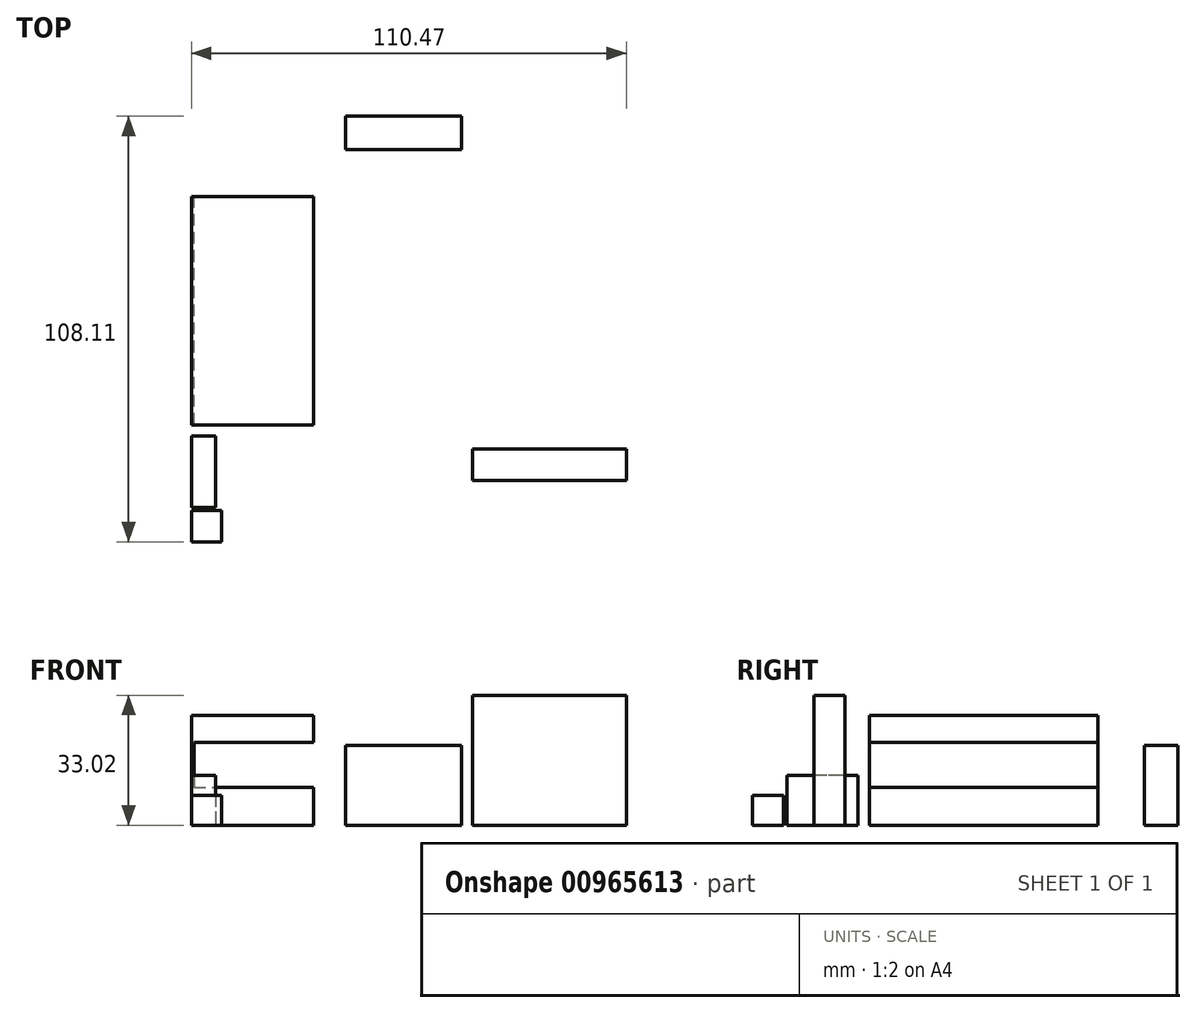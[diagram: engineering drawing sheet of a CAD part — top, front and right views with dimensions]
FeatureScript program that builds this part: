
annotation { "Feature Type Name" : "Feature", "Feature Type Description" : "" }
export const myFeature = defineFeature(function(context is Context, id is Id, definition is map)
    precondition{}
    {
        {
            var Q0;
            Q0=qCreatedBy(makeId("Top.planeOp"),FACE);
            var sketch = newSketch(context, id + "F0", { "sketchPlane" : qUnion([Q0])});
            skLineSegment(sketch, "E0", {"start": v(-79.8, -55.8) * mm, "end": v(-42.57, -55.8) * mm});
            skLineSegment(sketch, "E1", {"start": v(-42.57, -55.8) * mm, "end": v(-42.57, -57.97) * mm});
            skLineSegment(sketch, "E2", {"start": v(-42.57, -57.97) * mm, "end": v(-14.53, -57.97) * mm});
            skLineSegment(sketch, "E3", {"start": v(-14.53, -57.97) * mm, "end": v(-14.53, -55.8) * mm});
            skLineSegment(sketch, "E4", {"start": v(-14.53, -55.8) * mm, "end": v(-10.05, -55.8) * mm});
            skLineSegment(sketch, "E5", {"start": v(-10.05, -55.8) * mm, "end": v(-10.05, -38.6) * mm});
            skLineSegment(sketch, "E6", {"start": v(-10.05, -38.6) * mm, "end": v(30.69, -38.6) * mm});
            skLineSegment(sketch, "E7", {"start": v(30.69, -38.6) * mm, "end": v(30.69, -30.65) * mm});
            skLineSegment(sketch, "E8", {"start": v(30.69, -30.65) * mm, "end": v(33.75, -30.65) * mm});
            skLineSegment(sketch, "E9", {"start": v(33.75, -30.65) * mm, "end": v(33.75, 18.65) * mm});
            skLineSegment(sketch, "E10", {"start": v(33.75, 18.65) * mm, "end": v(30.69, 18.65) * mm});
            skLineSegment(sketch, "E11", {"start": v(30.69, 18.65) * mm, "end": v(30.69, 53.03) * mm});
            skLineSegment(sketch, "E12.bottom", {"start": v(-79.8, 33.53) * mm, "end": v(-48.74, 33.53) * mm});
            skLineSegment(sketch, "E12.top", {"start": v(-79.8, -24.5) * mm, "end": v(-48.74, -24.5) * mm});
            skLineSegment(sketch, "E12.left", {"start": v(-79.8, 33.53) * mm, "end": v(-79.8, -24.5) * mm});
            skLineSegment(sketch, "E12.right", {"start": v(-48.74, 33.53) * mm, "end": v(-48.74, -24.5) * mm});
            skLineSegment(sketch, "E13.bottom", {"start": v(-79.8, -27.35) * mm, "end": v(-73.64, -27.35) * mm});
            skLineSegment(sketch, "E13.top", {"start": v(-79.8, -45.45) * mm, "end": v(-73.64, -45.45) * mm});
            skLineSegment(sketch, "E13.left", {"start": v(-79.8, -27.35) * mm, "end": v(-79.8, -45.45) * mm});
            skLineSegment(sketch, "E13.right", {"start": v(-73.64, -27.35) * mm, "end": v(-73.64, -45.45) * mm});
            skLineSegment(sketch, "E14.bottom", {"start": v(-79.8, -46.32) * mm, "end": v(-72.1, -46.32) * mm});
            skLineSegment(sketch, "E14.top", {"start": v(-79.8, -54.22) * mm, "end": v(-72.1, -54.22) * mm});
            skLineSegment(sketch, "E14.left", {"start": v(-79.8, -46.32) * mm, "end": v(-79.8, -54.22) * mm});
            skLineSegment(sketch, "E14.right", {"start": v(-72.1, -46.32) * mm, "end": v(-72.1, -54.22) * mm});
            skPoint(sketch, "E15.firstSnap0", {"position": v(-72.1, -50.27) * mm});
            skLineSegment(sketch, "E16.bottom", {"start": v(-8.38, -38.6) * mm, "end": v(30.67, -38.6) * mm});
            skLineSegment(sketch, "E16.top", {"start": v(-8.38, -30.65) * mm, "end": v(30.67, -30.65) * mm});
            skLineSegment(sketch, "E16.left", {"start": v(-8.38, -38.6) * mm, "end": v(-8.38, -30.65) * mm});
            skLineSegment(sketch, "E16.right", {"start": v(30.67, -38.6) * mm, "end": v(30.67, -30.65) * mm});
            skLineSegment(sketch, "E17", {"start": v(-38.33, 54.66) * mm, "end": v(-79.8, 54.66) * mm});
            skLineSegment(sketch, "E18", {"start": v(30.69, 54.66) * mm, "end": v(30.69, 53.03) * mm});
            skLineSegment(sketch, "E19", {"start": v(-38.33, 56.29) * mm, "end": v(2.18, 56.29) * mm});
            skLineSegment(sketch, "E20", {"start": v(2.18, 56.29) * mm, "end": v(2.18, 54.66) * mm});
            skLineSegment(sketch, "E21", {"start": v(2.18, 54.66) * mm, "end": v(30.69, 54.66) * mm});
            skLineSegment(sketch, "E22", {"start": v(-38.33, 56.29) * mm, "end": v(-38.33, 54.66) * mm});
            skLineSegment(sketch, "E23.bottom", {"start": v(-40.63, 53.89) * mm, "end": v(-11.15, 53.89) * mm});
            skLineSegment(sketch, "E23.top", {"start": v(-40.63, 45.44) * mm, "end": v(-11.15, 45.44) * mm});
            skLineSegment(sketch, "E23.left", {"start": v(-40.63, 53.89) * mm, "end": v(-40.63, 45.44) * mm});
            skLineSegment(sketch, "E23.right", {"start": v(-11.15, 53.89) * mm, "end": v(-11.15, 45.44) * mm});
            skLineSegment(sketch, "E24", {"start": v(-79.8, 52.05) * mm, "end": v(-81.38, 52.05) * mm});
            skLineSegment(sketch, "E25", {"start": v(-81.38, 52.05) * mm, "end": v(-81.38, 35.03) * mm});
            skLineSegment(sketch, "E26", {"start": v(-81.38, 35.03) * mm, "end": v(-79.8, 35.03) * mm});
            skLineSegment(sketch, "E27", {"start": v(-79.8, 54.66) * mm, "end": v(-79.8, 52.05) * mm});
            skLineSegment(sketch, "E28", {"start": v(-79.8, 35.03) * mm, "end": v(-79.8, 33.53) * mm});
            skLineSegment(sketch, "E29", {"start": v(-79.8, -24.5) * mm, "end": v(-79.8, -27.35) * mm});
            skLineSegment(sketch, "E30", {"start": v(-79.8, -45.45) * mm, "end": v(-79.8, -46.32) * mm});
            skLineSegment(sketch, "E31", {"start": v(-79.8, -54.22) * mm, "end": v(-79.8, -55.8) * mm});
            skSolve(sketch);
        }
        {
            var Q0;
            Q0=makeQuery(id+"F0.imprint","IMPRINT",FACE,{"disambiguationData":[TD([[makeQuery(id+"F0.imprint","IMPRINT",EDGE,{"derivedFrom":sQuery(id+"F0.wireOp",EDGE,"E12.bottom")}),-1.0]])]});
            extrude(context, id + "F1", {"entities" : qUnion([Q0]), "depth" : 27.94 * mm, "offsetDistance" : 25.4 * mm});
        }
        {
            var Q0;
            Q0=makeQuery(id+"F0.imprint","IMPRINT",FACE,{"disambiguationData":[TD([[makeQuery(id+"F0.imprint","IMPRINT",EDGE,{"derivedFrom":sQuery(id+"F0.wireOp",EDGE,"E13.bottom")}),-1.0]])]});
            extrude(context, id + "F2", {"entities" : qUnion([Q0]), "depth" : 12.7 * mm, "offsetDistance" : 25.4 * mm});
        }
        {
            var Q0;
            Q0=makeQuery(id+"F0.imprint","IMPRINT",FACE,{"disambiguationData":[TD([[makeQuery(id+"F0.imprint","IMPRINT",EDGE,{"derivedFrom":sQuery(id+"F0.wireOp",EDGE,"E14.bottom")}),-1.0]])]});
            extrude(context, id + "F3", {"entities" : qUnion([Q0]), "depth" : 7.62 * mm, "offsetDistance" : 25.4 * mm});
        }
        {
            var Q0;
            Q0=makeQuery(id+"F0.imprint","IMPRINT",FACE,{"disambiguationData":[TD([[makeQuery(id+"F0.imprint","IMPRINT",EDGE,{"derivedFrom":sQuery(id+"F0.wireOp",EDGE,"E16.top")}),-1.0]])]});
            extrude(context, id + "F4", {"entities" : qUnion([Q0]), "depth" : 33.02 * mm, "offsetDistance" : 25.4 * mm});
        }
        {
            var Q0;
            Q0=makeQuery(id+"F0.imprint","IMPRINT",FACE,{"disambiguationData":[TD([[makeQuery(id+"F0.imprint","IMPRINT",EDGE,{"derivedFrom":sQuery(id+"F0.wireOp",EDGE,"E23.bottom")}),-1.0]])]});
            extrude(context, id + "F5", {"entities" : qUnion([Q0]), "depth" : 20.32 * mm, "offsetDistance" : 25.4 * mm});
        }
        {
            var Q0;
            Q0=makeQuery(id+"F1.opExtrude","SWEPT_FACE",FACE,{"disambiguationData":[OSD([sQuery(id+"F0.wireOp",EDGE,"E12.right")])]});
            var sketch = newSketch(context, id + "F6", { "sketchPlane" : qUnion([Q0])});
            skLineSegment(sketch, "E32.bottom", {"start": v(-24.5, 21.05) * mm, "end": v(33.53, 21.05) * mm});
            skLineSegment(sketch, "E32.top", {"start": v(-24.5, 9.65) * mm, "end": v(33.53, 9.65) * mm});
            skLineSegment(sketch, "E32.left", {"start": v(-24.5, 21.05) * mm, "end": v(-24.5, 9.65) * mm});
            skLineSegment(sketch, "E32.right", {"start": v(33.53, 21.05) * mm, "end": v(33.53, 9.65) * mm});
            skSolve(sketch);
        }
        {
            var Q0;
            Q0=makeQuery(id+"F6.imprint","IMPRINT",FACE,{"disambiguationData":[TD([[makeQuery(id+"F6.imprint","IMPRINT",EDGE,{"derivedFrom":sQuery(id+"F6.wireOp",EDGE,"E32.bottom")}),-1.0]])]});
            extrude(context, id + "F7", {"entities" : qUnion([Q0]), "operationType" : NewBodyOperationType.REMOVE, "oppositeDirection" : true, "depth" : 30.48 * mm, "offsetDistance" : 25.4 * mm});
        }
    });
